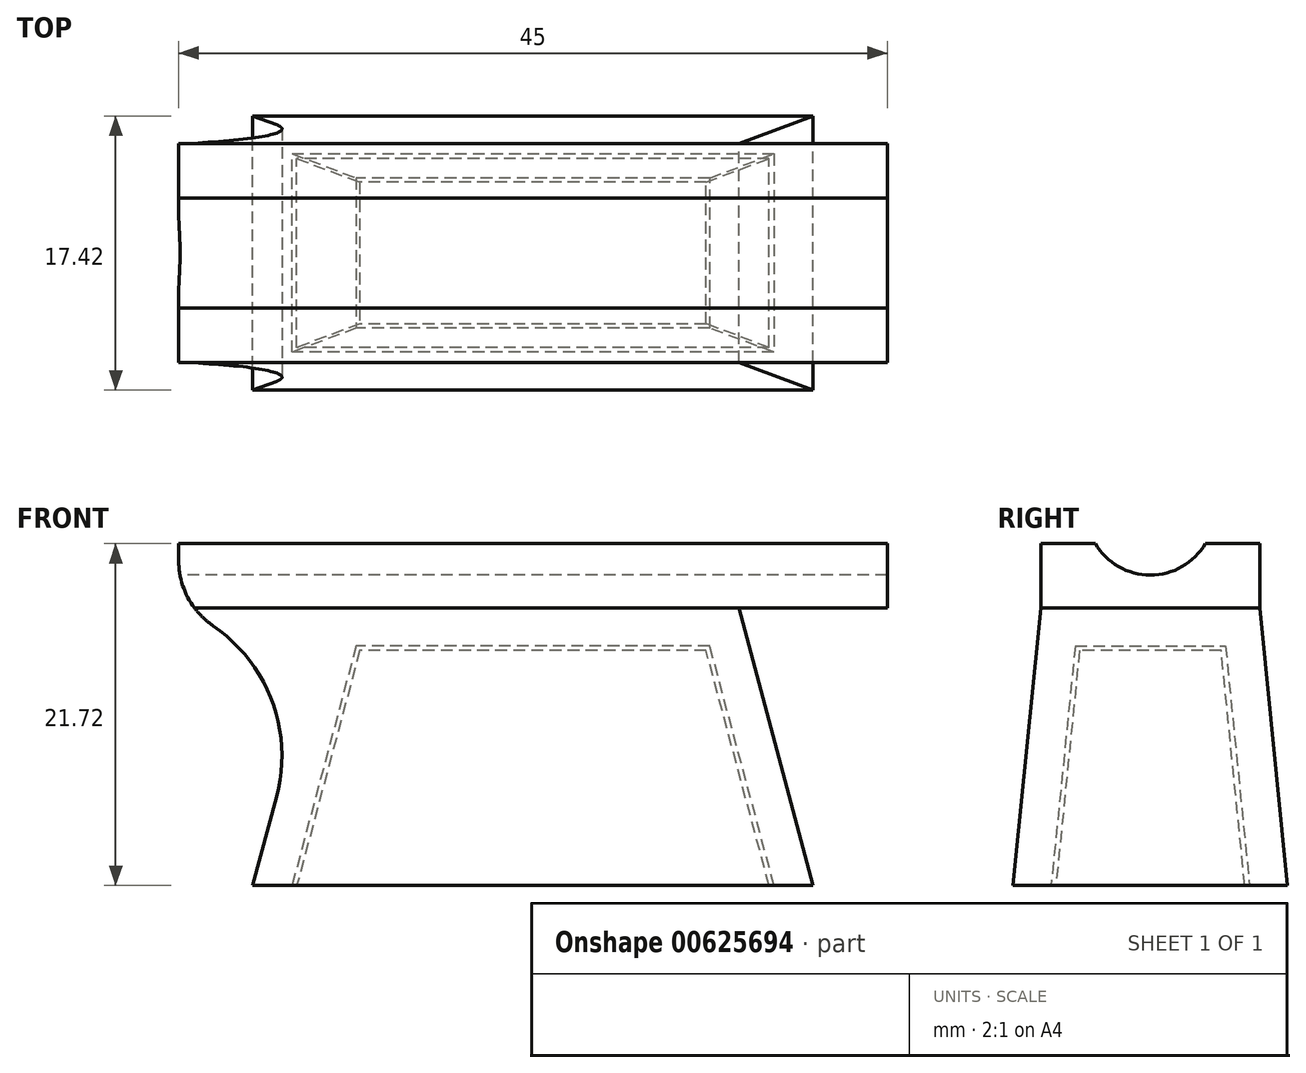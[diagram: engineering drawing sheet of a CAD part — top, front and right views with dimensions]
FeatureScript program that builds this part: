
annotation { "Feature Type Name" : "Feature", "Feature Type Description" : "" }
export const myFeature = defineFeature(function(context is Context, id is Id, definition is map)
    precondition{}
    {
        {
            var Q0;
            Q0=qCreatedBy(makeId("Right.planeOp"),FACE);
            var sketch = newSketch(context, id + "F0", { "sketchPlane" : qUnion([Q0])});
            skLineSegment(sketch, "E0", {"start": v(-6, 0) * mm, "end": v(6, 0) * mm});
            skLineSegment(sketch, "E1", {"start": v(6, 0) * mm, "end": v(4.5, 14.92) * mm});
            skLineSegment(sketch, "E2", {"start": v(4.5, 14.92) * mm, "end": v(-4.5, 14.92) * mm});
            skLineSegment(sketch, "E3", {"start": v(-4.5, 14.92) * mm, "end": v(-6, 0) * mm});
            skPoint(sketch, "E4", {"position": v(0, 0) * mm});
            skPoint(sketch, "E5", {"position": v(0, 14.92) * mm});
            skSolve(sketch);
        }
        {
            var Q0;
            Q0=makeQuery(id+"F0.imprint","IMPRINT",FACE,{"disambiguationData":[TD([[makeQuery(id+"F0.imprint","IMPRINT",EDGE,{"derivedFrom":sQuery(id+"F0.wireOp",EDGE,"E0")}),1.0]])]});
            extrude(context, id + "F1", {"entities" : qUnion([Q0]), "depth" : 15 * mm, "offsetDistance" : 25 * mm, "hasSecondDirection" : true, "secondDirectionOppositeDirection" : true, "secondDirectionDepth" : 15 * mm});
        }
        {
            var Q0;
            Q0=makeQuery(id+"F1.opExtrude","CAP_EDGE",EDGE,{"disambiguationData":[OSD([sQuery(id+"F0.wireOp",EDGE,"E0")])],"isStart":true});
            cPlane(context, id + "F2", {"entities" : qUnion([Q0]), "cplaneType" : CPlaneType.LINE_ANGLE, "offset" : 1.1 * mm, "angle" : 255 * degree, "oppositeDirection" : true, "width" : 150 * mm, "height" : 150 * mm});
        }
        {
            var Q0;
            Q0=qCreatedBy(makeId("Right.planeOp"),FACE);
            cPlane(context, id + "F3", {"entities" : qUnion([Q0]), "cplaneType" : CPlaneType.OFFSET, "offset" : 11 * mm, "oppositeDirection" : true, "width" : 150 * mm, "height" : 150 * mm});
        }
        {
            var Q0;
            Q0=makeQuery(id+"F1.opExtrude","CAP_EDGE",EDGE,{"disambiguationData":[OSD([sQuery(id+"F0.wireOp",EDGE,"E0")])],"isStart":false});
            cPlane(context, id + "F4", {"entities" : qUnion([Q0]), "cplaneType" : CPlaneType.LINE_ANGLE, "offset" : 25 * mm, "angle" : 255 * degree, "width" : 150 * mm, "height" : 150 * mm});
        }
        {
            var Q0;
            Q0=qCreatedBy(id+"F4.planeOp",FACE);
            var sketch = newSketch(context, id + "F5", { "sketchPlane" : qUnion([Q0])});
            skLineSegment(sketch, "E6.bottom", {"start": v(7.81, 12.39) * mm, "end": v(-8.95, 12.39) * mm});
            skLineSegment(sketch, "E6.top", {"start": v(7.81, -4.44) * mm, "end": v(-8.95, -4.44) * mm});
            skLineSegment(sketch, "E6.left", {"start": v(7.81, 12.39) * mm, "end": v(7.81, -4.44) * mm});
            skLineSegment(sketch, "E6.right", {"start": v(-8.95, 12.39) * mm, "end": v(-8.95, -4.44) * mm});
            skSolve(sketch);
        }
        {
            var Q0;
            Q0 = qSketchRegion(id + "F5", true);
            extrude(context, id + "F6", {"entities" : qUnion([Q0]), "operationType" : NewBodyOperationType.REMOVE, "oppositeDirection" : true, "depth" : 10 * mm, "offsetDistance" : 25 * mm});
        }
        {
            var Q0;
            Q0=qCreatedBy(id+"F2.planeOp",FACE);
            var sketch = newSketch(context, id + "F7", { "sketchPlane" : qUnion([Q0])});
            skLineSegment(sketch, "E7.bottom", {"start": v(8.24, 13.32) * mm, "end": v(-9.59, 13.32) * mm});
            skLineSegment(sketch, "E7.top", {"start": v(8.24, -6.15) * mm, "end": v(-9.59, -6.15) * mm});
            skLineSegment(sketch, "E7.left", {"start": v(8.24, 13.32) * mm, "end": v(8.24, -6.15) * mm});
            skLineSegment(sketch, "E7.right", {"start": v(-9.59, 13.32) * mm, "end": v(-9.59, -6.15) * mm});
            skSolve(sketch);
        }
        {
            var Q0;
            Q0 = qSketchRegion(id + "F7", true);
            extrude(context, id + "F8", {"entities" : qUnion([Q0]), "operationType" : NewBodyOperationType.REMOVE, "oppositeDirection" : true, "depth" : 10 * mm, "offsetDistance" : 25 * mm});
        }
        {
            var Q0;
            Q0=makeQuery(id+"F1.opExtrude","SWEPT_BODY",BODY,{"disambiguationData":[OSD([sQuery(id+"F0.wireOp",EDGE,"E0"),sQuery(id+"F0.wireOp",EDGE,"E1"),sQuery(id+"F0.wireOp",EDGE,"E2"),sQuery(id+"F0.wireOp",EDGE,"E3")])]});
            transform(context, id + "F9", {"entities" : qUnion([Q0]), "transformType" : TransformType.COPY});
        }
        {
            var Q0;
            Q0=makeQuery(id+"F9.opPattern","COPY",FACE,{"derivedFrom":makeQuery(id+"F1.opExtrude","SWEPT_FACE",FACE,{"disambiguationData":[OSD([sQuery(id+"F0.wireOp",EDGE,"E0")])]}),"instanceName":"1"});
            var Q1;
            Q1=makeQuery(id+"F9.opPattern","COPY",BODY,{"derivedFrom":makeQuery(id+"F1.opExtrude","SWEPT_BODY",BODY,{"disambiguationData":[OSD([sQuery(id+"F0.wireOp",EDGE,"E0"),sQuery(id+"F0.wireOp",EDGE,"E1"),sQuery(id+"F0.wireOp",EDGE,"E2"),sQuery(id+"F0.wireOp",EDGE,"E3")])]}),"instanceName":"1"});
            shell(context, id + "F10", {"isHollow" : true, "entities" : qUnion([Q0]), "parts" : qUnion([Q1]), "thickness" : .3 * mm, "oppositeDirection" : true});
        }
        {
            var Q0;
            Q0=makeQuery(id+"F1.opExtrude","SWEPT_BODY",BODY,{"disambiguationData":[OSD([sQuery(id+"F0.wireOp",EDGE,"E0"),sQuery(id+"F0.wireOp",EDGE,"E1"),sQuery(id+"F0.wireOp",EDGE,"E2"),sQuery(id+"F0.wireOp",EDGE,"E3")])]});
            transform(context, id + "F11", {"entities" : qUnion([Q0]), "transformType" : TransformType.COPY});
        }
        {
            var Q0;
            Q0=makeQuery(id+"F11.opPattern","COPY",FACE,{"derivedFrom":makeQuery(id+"F1.opExtrude","SWEPT_FACE",FACE,{"disambiguationData":[OSD([sQuery(id+"F0.wireOp",EDGE,"E0")])]}),"instanceName":"1"});
            shell(context, id + "F12", {"entities" : qUnion([Q0]), "thickness" : (2.5 + .2) * mm, "oppositeDirection" : true});
        }
        {
            var Q0;
            Q0=makeQuery(id+"F9.opPattern","COPY",BODY,{"derivedFrom":makeQuery(id+"F1.opExtrude","SWEPT_BODY",BODY,{"disambiguationData":[OSD([sQuery(id+"F0.wireOp",EDGE,"E0"),sQuery(id+"F0.wireOp",EDGE,"E1"),sQuery(id+"F0.wireOp",EDGE,"E2"),sQuery(id+"F0.wireOp",EDGE,"E3")])]}),"instanceName":"1"});
            var Q1;
            Q1=makeQuery(id+"F11.opPattern","COPY",BODY,{"derivedFrom":makeQuery(id+"F1.opExtrude","SWEPT_BODY",BODY,{"disambiguationData":[OSD([sQuery(id+"F0.wireOp",EDGE,"E0"),sQuery(id+"F0.wireOp",EDGE,"E1"),sQuery(id+"F0.wireOp",EDGE,"E2"),sQuery(id+"F0.wireOp",EDGE,"E3")])]}),"instanceName":"1"});
            booleanBodies(context, id + "F13", {"operationType" : BooleanOperationType.SUBTRACTION, "tools" : qUnion([Q0]), "targets" : qUnion([Q1])});
        }
        {
            var Q0;
            Q0=makeQuery(id+"F11.opPattern","COPY",FACE,{"derivedFrom":makeQuery(id+"F1.opExtrude","SWEPT_FACE",FACE,{"disambiguationData":[OSD([sQuery(id+"F0.wireOp",EDGE,"E2")])]}),"instanceName":"1"});
            cPlane(context, id + "F14", {"entities" : qUnion([Q0]), "cplaneType" : CPlaneType.OFFSET, "offset" : 0 * mm, "width" : 150 * mm, "height" : 150 * mm});
        }
        {
            var Q0;
            Q0=qCreatedBy(id+"F14.planeOp",FACE);
            var sketch = newSketch(context, id + "F15", { "sketchPlane" : qUnion([Q0])});
            skLineSegment(sketch, "E8.bottom", {"start": v(-22.5, -6.94) * mm, "end": v(22.5, -6.94) * mm});
            skLineSegment(sketch, "E8.top", {"start": v(-22.5, 6.94) * mm, "end": v(22.5, 6.94) * mm});
            skLineSegment(sketch, "E8.left", {"start": v(-22.5, -6.94) * mm, "end": v(-22.5, 6.94) * mm});
            skLineSegment(sketch, "E8.right", {"start": v(22.5, -6.94) * mm, "end": v(22.5, 6.94) * mm});
            skPoint(sketch, "E8.middle", {"position": v(0, 0) * mm});
            skSolve(sketch);
        }
        {
            var Q0;
            Q0 = qSketchRegion(id + "F15", true);
            extrude(context, id + "F16", {"entities" : qUnion([Q0]), "operationType" : NewBodyOperationType.ADD, "depth" : 4.1 * mm, "offsetDistance" : 25 * mm});
        }
        {
            var Q0;
            Q0=makeQuery(id+"F16.opExtrude","SWEPT_FACE",FACE,{"disambiguationData":[OSD([sQuery(id+"F15.wireOp",EDGE,"E8.left")])]});
            cPlane(context, id + "F17", {"entities" : qUnion([Q0]), "cplaneType" : CPlaneType.OFFSET, "offset" : 0 * mm, "width" : 150 * mm, "height" : 150 * mm});
        }
        {
            var Q0;
            Q0=qCreatedBy(id+"F17.planeOp",FACE);
            var sketch = newSketch(context, id + "F18", { "sketchPlane" : qUnion([Q0])});
            skLineSegment(sketch, "E9", {"start": v(0, 29.2) * mm, "end": v(0, 11.15) * mm, "construction": true});
            skPoint(sketch, "E10", {"position": v(-3.5, 21.72) * mm});
            skPoint(sketch, "E11", {"position": v(3.5, 21.72) * mm});
            skPoint(sketch, "E12", {"position": v(0, 19.72) * mm});
            skArc(sketch, "E13", {"start": v(-3.5, 21.72) * mm, "mid": v(0, 19.72) * mm, "end": v(3.5, 21.72) * mm});
            skLineSegment(sketch, "E14", {"start": v(3.5, 21.72) * mm, "end": v(-3.5, 21.72) * mm});
            skSolve(sketch);
        }
        {
            var Q0;
            Q0=makeQuery(id+"F18.imprint","IMPRINT",FACE,{"disambiguationData":[TD([[makeQuery(id+"F18.imprint","IMPRINT",EDGE,{"derivedFrom":sQuery(id+"F18.wireOp",EDGE,"E13")}),1.0]])]});
            extrude(context, id + "F19", {"entities" : qUnion([Q0]), "operationType" : NewBodyOperationType.REMOVE, "endBound" : BoundingType.THROUGH_ALL, "oppositeDirection" : true, "depth" : 25 * mm, "offsetDistance" : 25 * mm});
        }
        {
            var Q0;
            Q0=makeQuery(id+"F11.opPattern","COPY",EDGE,{"derivedFrom":makeQuery(id+"F6.boolean.opBoolean","INTERSECT",EDGE,{"derivedFrom":[makeQuery(id+"F1.opExtrude","SWEPT_FACE",FACE,{"disambiguationData":[OSD([sQuery(id+"F0.wireOp",EDGE,"E2")])]}),makeQuery(id+"F6.opExtrude","CAP_FACE",FACE,{"disambiguationData":[OSD([sQuery(id+"F5.wireOp",EDGE,"E6.bottom"),sQuery(id+"F5.wireOp",EDGE,"E6.top"),sQuery(id+"F5.wireOp",EDGE,"E6.left"),sQuery(id+"F5.wireOp",EDGE,"E6.right")])],"isStart":true})]}),"instanceName":"1"});
            var Q1;
            Q1=makeQuery(id+"F11.opPattern","COPY",EDGE,{"derivedFrom":makeQuery(id+"F8.boolean.opBoolean","INTERSECT",EDGE,{"derivedFrom":[makeQuery(id+"F1.opExtrude","SWEPT_FACE",FACE,{"disambiguationData":[OSD([sQuery(id+"F0.wireOp",EDGE,"E2")])]}),makeQuery(id+"F8.opExtrude","CAP_FACE",FACE,{"disambiguationData":[OSD([sQuery(id+"F7.wireOp",EDGE,"E7.bottom"),sQuery(id+"F7.wireOp",EDGE,"E7.top"),sQuery(id+"F7.wireOp",EDGE,"E7.left"),sQuery(id+"F7.wireOp",EDGE,"E7.right")])],"isStart":true})]}),"instanceName":"1"});
            fillet(context, id + "F20", {"entities" : qUnion([Q0, Q1]), "radius" : 10 * mm, "tangentPropagation" : true, "allowEdgeOverflow" : false});
        }
        {
            var Q0;
            Q0=makeQuery(id+"F20.opFillet","BLEND_EDGE",EDGE,{"blendedFrom":[makeQuery(id+"F11.opPattern","COPY",EDGE,{"derivedFrom":makeQuery(id+"F8.boolean.opBoolean","INTERSECT",EDGE,{"derivedFrom":[makeQuery(id+"F1.opExtrude","SWEPT_FACE",FACE,{"disambiguationData":[OSD([sQuery(id+"F0.wireOp",EDGE,"E2")])]}),makeQuery(id+"F8.opExtrude","CAP_FACE",FACE,{"disambiguationData":[OSD([sQuery(id+"F7.wireOp",EDGE,"E7.bottom"),sQuery(id+"F7.wireOp",EDGE,"E7.top"),sQuery(id+"F7.wireOp",EDGE,"E7.left"),sQuery(id+"F7.wireOp",EDGE,"E7.right")])],"isStart":true})]}),"instanceName":"1"}),makeQuery(id+"F16.opExtrude","SWEPT_FACE",FACE,{"disambiguationData":[OSD([sQuery(id+"F15.wireOp",EDGE,"E8.left")])]})],"blendedInto":[makeQuery(id+"F16.opExtrude","SWEPT_FACE",FACE,{"disambiguationData":[OSD([sQuery(id+"F15.wireOp",EDGE,"E8.left")])]})]});
            var Q1;
            Q1=makeQuery(id+"F20.opFillet","BLEND_EDGE",EDGE,{"blendedFrom":[makeQuery(id+"F11.opPattern","COPY",EDGE,{"derivedFrom":makeQuery(id+"F6.boolean.opBoolean","INTERSECT",EDGE,{"derivedFrom":[makeQuery(id+"F1.opExtrude","SWEPT_FACE",FACE,{"disambiguationData":[OSD([sQuery(id+"F0.wireOp",EDGE,"E2")])]}),makeQuery(id+"F6.opExtrude","CAP_FACE",FACE,{"disambiguationData":[OSD([sQuery(id+"F5.wireOp",EDGE,"E6.bottom"),sQuery(id+"F5.wireOp",EDGE,"E6.top"),sQuery(id+"F5.wireOp",EDGE,"E6.left"),sQuery(id+"F5.wireOp",EDGE,"E6.right")])],"isStart":true})]}),"instanceName":"1"}),makeQuery(id+"F16.opExtrude","SWEPT_FACE",FACE,{"disambiguationData":[OSD([sQuery(id+"F15.wireOp",EDGE,"E8.right")])]})],"blendedInto":[makeQuery(id+"F16.opExtrude","SWEPT_FACE",FACE,{"disambiguationData":[OSD([sQuery(id+"F15.wireOp",EDGE,"E8.right")])]})]});
            fillet(context, id + "F21", {"entities" : qUnion([Q0, Q1]), "radius" : 5 * mm, "tangentPropagation" : true, "allowEdgeOverflow" : false});
        }
    });
